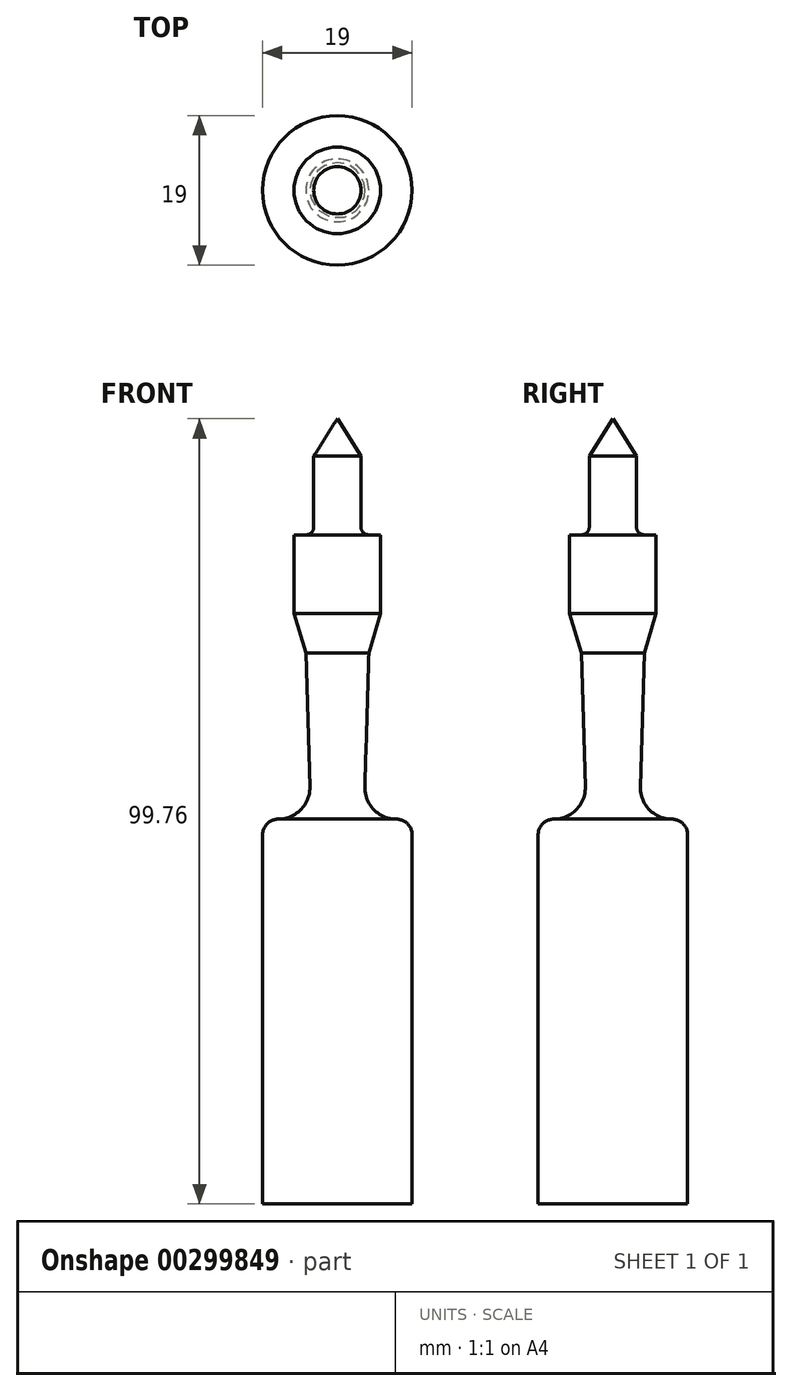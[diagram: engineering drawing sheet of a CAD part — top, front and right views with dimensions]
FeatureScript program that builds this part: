
annotation { "Feature Type Name" : "Feature", "Feature Type Description" : "" }
export const myFeature = defineFeature(function(context is Context, id is Id, definition is map)
    precondition{}
    {
        {
            var Q0;
            Q0=qCreatedBy(makeId("Front.planeOp"),FACE);
            var sketch = newSketch(context, id + "F0", { "sketchPlane" : qUnion([Q0])});
            skLineSegment(sketch, "E0", {"start": v(0, 0) * mm, "end": v(0, -100) * mm});
            skLineSegment(sketch, "E1", {"start": v(3, -5) * mm, "end": v(3, -14) * mm});
            skArc(sketch, "E2", {"start": v(3, -14) * mm, "mid": v(3.3, -14.7) * mm, "end": v(4, -15) * mm});
            skLineSegment(sketch, "E3", {"start": v(0, 0) * mm, "end": v(17.27, 0) * mm, "construction": true});
            skLineSegment(sketch, "E4", {"start": v(4, -15) * mm, "end": v(5.5, -15) * mm});
            skLineSegment(sketch, "E5", {"start": v(5.5, -15) * mm, "end": v(5.5, -25) * mm});
            skLineSegment(sketch, "E6", {"start": v(5.5, -25) * mm, "end": v(4, -30) * mm});
            skLineSegment(sketch, "E7", {"start": v(4, -30) * mm, "end": v(3.5, -47) * mm});
            skArc(sketch, "E8", {"start": v(3.5, -47) * mm, "mid": v(4.63, -49.9) * mm, "end": v(7.5, -51.12) * mm});
            skArc(sketch, "E9", {"start": v(9.5, -53.12) * mm, "mid": v(8.91, -51.7) * mm, "end": v(7.5, -51.12) * mm});
            skLineSegment(sketch, "E10", {"start": v(9.5, -53.12) * mm, "end": v(9.5, -100) * mm});
            skLineSegment(sketch, "E11", {"start": v(0, -100) * mm, "end": v(9.5, -100) * mm});
            skLineSegment(sketch, "E12", {"start": v(-0.15, 0) * mm, "end": v(3, -5) * mm});
            skSolve(sketch);
        }
        {
            var Q0;
            Q0 = qSketchRegion(id + "F0", true);
            var Q1;
            Q1=sQuery(id+"F0.wireOp",EDGE,"E0");
            revolve(context, id + "F1", {"entities" : qUnion([Q0]), "axis" : qUnion([Q1]), "revolveType" : RevolveType.FULL});
        }
    });
